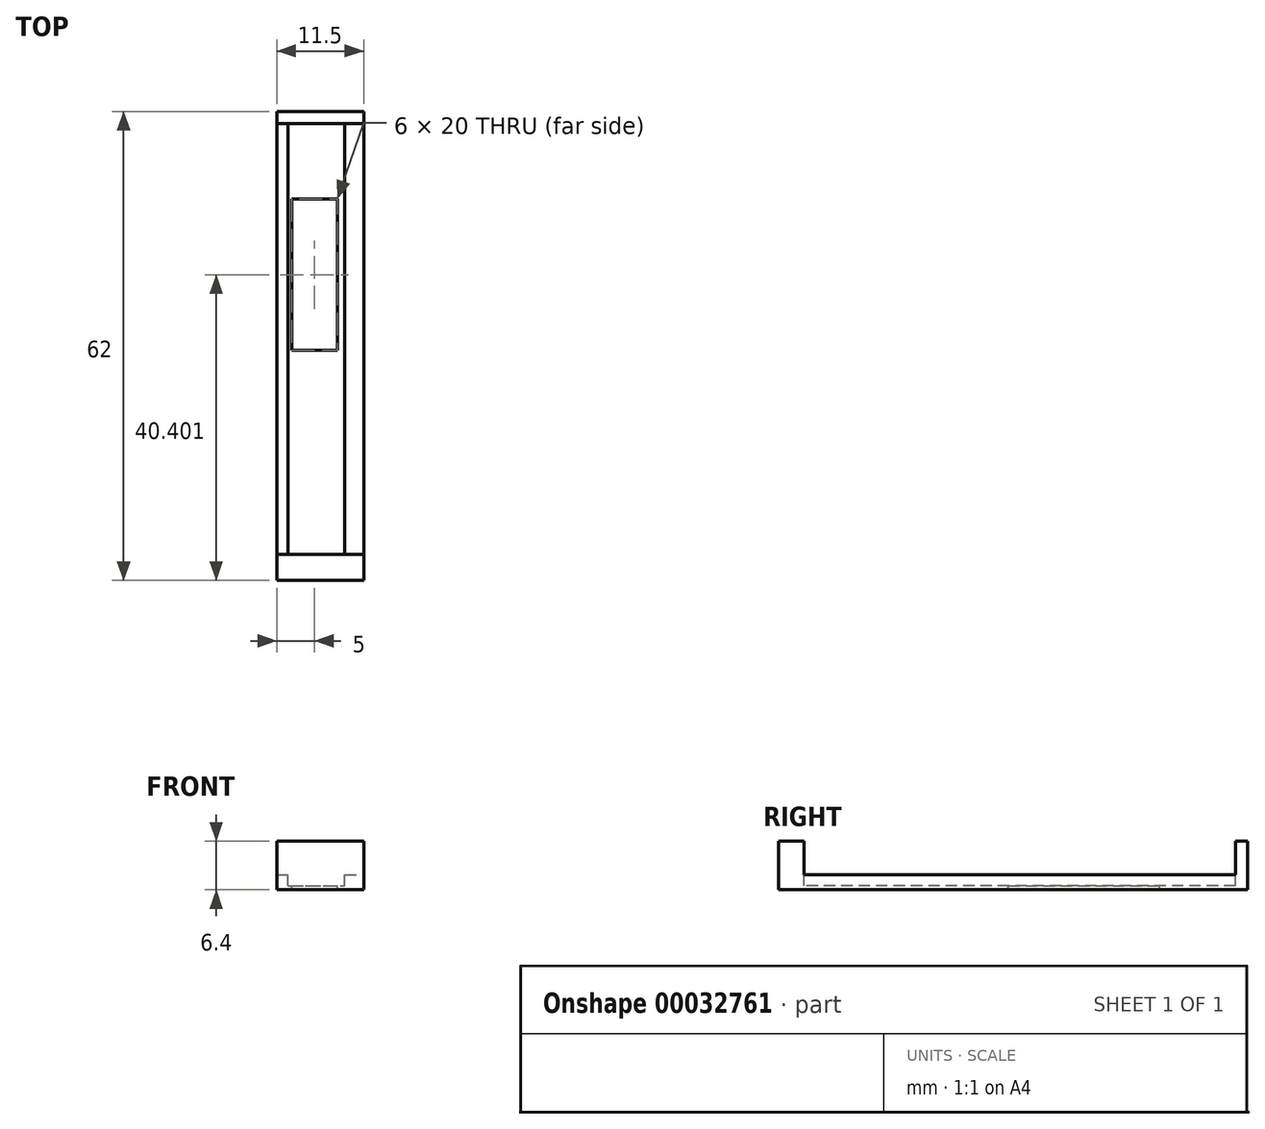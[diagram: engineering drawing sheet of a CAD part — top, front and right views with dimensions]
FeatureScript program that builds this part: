
annotation { "Feature Type Name" : "Feature", "Feature Type Description" : "" }
export const myFeature = defineFeature(function(context is Context, id is Id, definition is map)
    precondition{}
    {
        {
            var Q0;
            Q0=qCreatedBy(makeId("Top.planeOp"),FACE);
            var sketch = newSketch(context, id + "F0", { "sketchPlane" : qUnion([Q0])});
            skLineSegment(sketch, "E0.bottom", {"start": v(-5.75, 30.36) * mm, "end": v(5.75, 30.36) * mm});
            skLineSegment(sketch, "E0.top", {"start": v(-5.75, -31.64) * mm, "end": v(5.75, -31.64) * mm});
            skLineSegment(sketch, "E0.left", {"start": v(-5.75, 30.36) * mm, "end": v(-5.75, -31.64) * mm});
            skLineSegment(sketch, "E0.right", {"start": v(5.75, 30.36) * mm, "end": v(5.75, -31.64) * mm});
            skLineSegment(sketch, "E1", {"start": v(0, 30.36) * mm, "end": v(0, -31.64) * mm, "construction": true});
            skLineSegment(sketch, "E2", {"start": v(-5.75, -0.64) * mm, "end": v(5.75, -0.64) * mm, "construction": true});
            skLineSegment(sketch, "E3", {"start": v(5.75, -0.64) * mm, "end": v(5.5, -1.97) * mm, "construction": true});
            skSolve(sketch);
        }
        {
            var Q0;
            Q0=makeQuery(id+"F0.imprint","IMPRINT",FACE,{"disambiguationData":[TD([[makeQuery(id+"F0.imprint","IMPRINT",EDGE,{"derivedFrom":sQuery(id+"F0.wireOp",EDGE,"E0.bottom")}),-1.0]])]});
            extrude(context, id + "F1", {"entities" : qUnion([Q0]), "depth" : 2 * mm});
        }
        {
            var Q0;
            Q0=makeQuery(id+"F1.opExtrude","CAP_FACE",FACE,{"disambiguationData":[OSD([sQuery(id+"F0.wireOp",EDGE,"E0.bottom"),sQuery(id+"F0.wireOp",EDGE,"E0.top"),sQuery(id+"F0.wireOp",EDGE,"E0.left"),sQuery(id+"F0.wireOp",EDGE,"E0.right")])],"isStart":false});
            var sketch = newSketch(context, id + "F2", { "sketchPlane" : qUnion([Q0])});
            skLineSegment(sketch, "E4.bottom", {"start": v(-4.25, 28.76) * mm, "end": v(3.25, 28.76) * mm});
            skLineSegment(sketch, "E4.top", {"start": v(-4.25, -28.24) * mm, "end": v(3.25, -28.24) * mm});
            skLineSegment(sketch, "E4.left", {"start": v(-4.25, 28.76) * mm, "end": v(-4.25, -28.24) * mm});
            skLineSegment(sketch, "E4.right", {"start": v(3.25, 28.76) * mm, "end": v(3.25, -28.24) * mm});
            skLineSegment(sketch, "E5", {"start": v(-2.12, -31.64) * mm, "end": v(-2.12, -28.24) * mm, "construction": true});
            skLineSegment(sketch, "E6", {"start": v(3.25, -23.7) * mm, "end": v(5.75, -23.7) * mm, "construction": true});
            skSolve(sketch);
        }
        {
            var Q0;
            Q0 = qSketchRegion(id + "F2", true);
            extrude(context, id + "F3", {"entities" : qUnion([Q0]), "operationType" : NewBodyOperationType.REMOVE, "oppositeDirection" : true, "depth" : 1.5 * mm});
        }
        {
            var Q0;
            Q0=makeQuery(id+"F3.boolean.opBoolean","COPY",FACE,{"derivedFrom":makeQuery(id+"F3.opExtrude","CAP_FACE",FACE,{"disambiguationData":[OSD([sQuery(id+"F2.wireOp",EDGE,"E4.bottom"),sQuery(id+"F2.wireOp",EDGE,"E4.top"),sQuery(id+"F2.wireOp",EDGE,"E4.left"),sQuery(id+"F2.wireOp",EDGE,"E4.right")])],"isStart":false})});
            var sketch = newSketch(context, id + "F4", { "sketchPlane" : qUnion([Q0])});
            skLineSegment(sketch, "E7.bottom", {"start": v(-3.75, -1.24) * mm, "end": v(2.25, -1.24) * mm});
            skLineSegment(sketch, "E7.top", {"start": v(-3.75, 18.76) * mm, "end": v(2.25, 18.76) * mm});
            skLineSegment(sketch, "E7.left", {"start": v(-3.75, -1.24) * mm, "end": v(-3.75, 18.76) * mm});
            skLineSegment(sketch, "E7.right", {"start": v(2.25, -1.24) * mm, "end": v(2.25, 18.76) * mm});
            skLineSegment(sketch, "E8", {"start": v(2.25, 8.76) * mm, "end": v(-3.75, 8.76) * mm, "construction": true});
            skLineSegment(sketch, "E9", {"start": v(1.13, 8.76) * mm, "end": v(1.13, 28.76) * mm, "construction": true});
            skSolve(sketch);
        }
        {
            var Q0;
            Q0=makeQuery(id+"F4.imprint","IMPRINT",FACE,{"disambiguationData":[TD([[makeQuery(id+"F4.imprint","IMPRINT",EDGE,{"derivedFrom":sQuery(id+"F4.wireOp",EDGE,"E7.bottom")}),1.0]])]});
            var Q1;
            Q1=makeQuery(id+"F1.opExtrude","CAP_FACE",FACE,{"disambiguationData":[OSD([sQuery(id+"F0.wireOp",EDGE,"E0.bottom"),sQuery(id+"F0.wireOp",EDGE,"E0.top"),sQuery(id+"F0.wireOp",EDGE,"E0.left"),sQuery(id+"F0.wireOp",EDGE,"E0.right")])],"isStart":true});
            extrude(context, id + "F5", {"entities" : qUnion([Q0]), "operationType" : NewBodyOperationType.REMOVE, "endBound" : BoundingType.UP_TO_SURFACE, "oppositeDirection" : true, "endBoundEntityFace" : qUnion([Q1]), "depth" : 25 * mm});
        }
        {
            var Q0;
            Q0=makeQuery(id+"F1.opExtrude","CAP_FACE",FACE,{"disambiguationData":[OSD([sQuery(id+"F0.wireOp",EDGE,"E0.bottom"),sQuery(id+"F0.wireOp",EDGE,"E0.top"),sQuery(id+"F0.wireOp",EDGE,"E0.left"),sQuery(id+"F0.wireOp",EDGE,"E0.right")])],"isStart":false});
            var sketch = newSketch(context, id + "F6", { "sketchPlane" : qUnion([Q0])});
            skLineSegment(sketch, "E10.bottom", {"start": v(-5.75, -31.64) * mm, "end": v(5.75, -31.64) * mm});
            skLineSegment(sketch, "E10.top", {"start": v(-5.75, -28.24) * mm, "end": v(5.75, -28.24) * mm});
            skLineSegment(sketch, "E10.left", {"start": v(-5.75, -31.64) * mm, "end": v(-5.75, -28.24) * mm});
            skLineSegment(sketch, "E10.right", {"start": v(5.75, -31.64) * mm, "end": v(5.75, -28.24) * mm});
            skLineSegment(sketch, "E11.bottom", {"start": v(-5.75, 28.76) * mm, "end": v(5.75, 28.76) * mm});
            skLineSegment(sketch, "E11.top", {"start": v(-5.75, 30.36) * mm, "end": v(5.75, 30.36) * mm});
            skLineSegment(sketch, "E11.left", {"start": v(-5.75, 28.76) * mm, "end": v(-5.75, 30.36) * mm});
            skLineSegment(sketch, "E11.right", {"start": v(5.75, 28.76) * mm, "end": v(5.75, 30.36) * mm});
            skSolve(sketch);
        }
        {
            var Q0;
            Q0=makeQuery(id+"F6.imprint","IMPRINT",FACE,{"disambiguationData":[TD([[makeQuery(id+"F6.imprint","IMPRINT",EDGE,{"derivedFrom":sQuery(id+"F6.wireOp",EDGE,"E10.bottom")}),1.0]])]});
            var Q1;
            Q1=makeQuery(id+"F6.imprint","IMPRINT",FACE,{"disambiguationData":[TD([[makeQuery(id+"F6.imprint","IMPRINT",EDGE,{"derivedFrom":sQuery(id+"F6.wireOp",EDGE,"E11.top")}),-1.0]])]});
            extrude(context, id + "F7", {"entities" : qUnion([Q0, Q1]), "operationType" : NewBodyOperationType.ADD, "depth" : 4.4 * mm});
        }
    });
